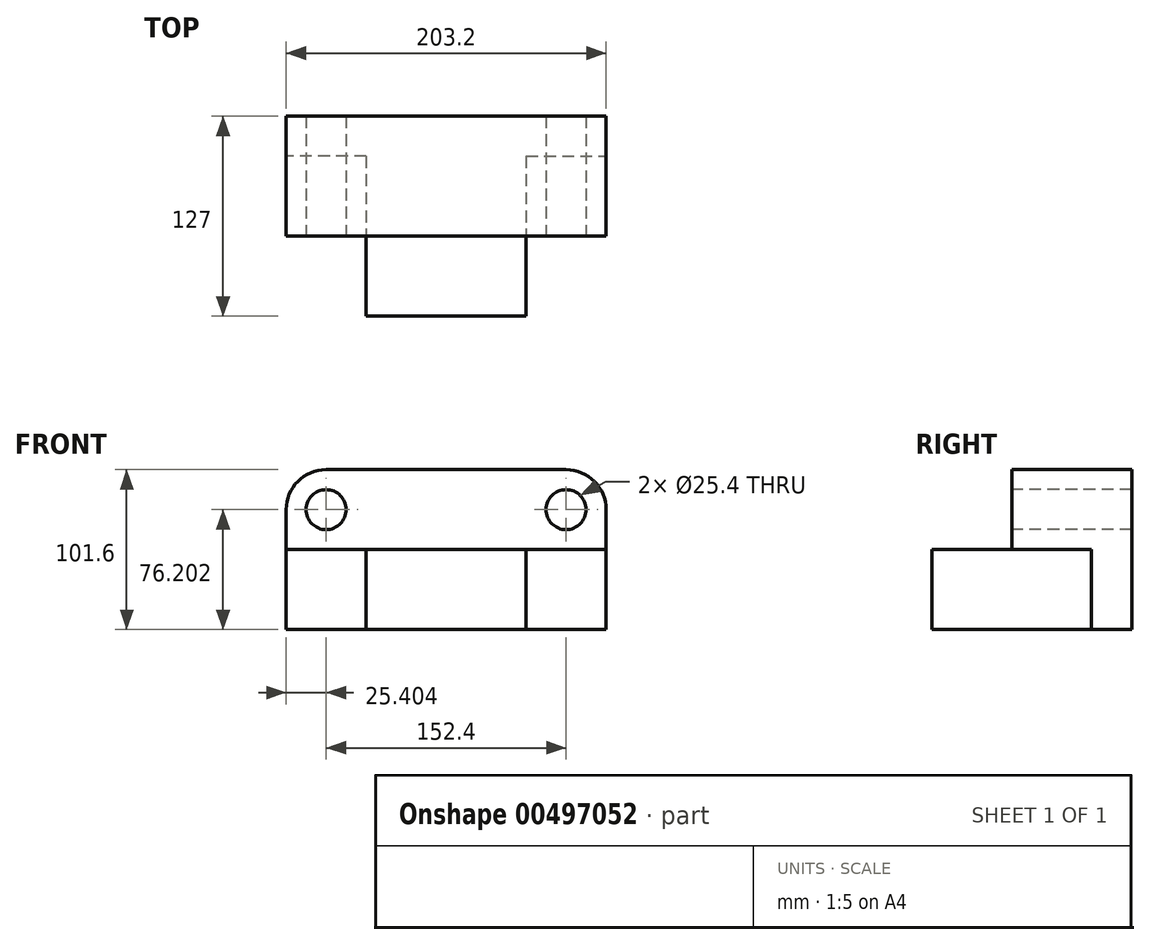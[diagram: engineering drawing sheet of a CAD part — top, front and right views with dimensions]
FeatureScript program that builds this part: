
annotation { "Feature Type Name" : "Feature", "Feature Type Description" : "" }
export const myFeature = defineFeature(function(context is Context, id is Id, definition is map)
    precondition{}
    {
        {
            var Q0;
            Q0=qCreatedBy(makeId("Front.planeOp"),FACE);
            var sketch = newSketch(context, id + "F0", { "sketchPlane" : qUnion([Q0])});
            skLineSegment(sketch, "E0", {"start": v(-74.58, -52.28) * mm, "end": v(128.62, -52.28) * mm});
            skLineSegment(sketch, "E1", {"start": v(128.62, -52.28) * mm, "end": v(128.62, 49.32) * mm});
            skLineSegment(sketch, "E2", {"start": v(128.62, 49.32) * mm, "end": v(-74.58, 49.32) * mm});
            skLineSegment(sketch, "E3", {"start": v(-74.58, 49.32) * mm, "end": v(-74.58, -52.28) * mm});
            skSolve(sketch);
        }
        {
            var Q0;
            Q0=makeQuery(id+"F0.imprint","IMPRINT",FACE,{"disambiguationData":[TD([[makeQuery(id+"F0.imprint","IMPRINT",EDGE,{"derivedFrom":sQuery(id+"F0.wireOp",EDGE,"E0")}),1.0]])]});
            extrude(context, id + "F1", {"entities" : qUnion([Q0]), "depth" : 76.2 * mm});
        }
        {
            var Q0;
            Q0=makeQuery(id+"F1.opExtrude","CAP_FACE",FACE,{"disambiguationData":[OSD([sQuery(id+"F0.wireOp",EDGE,"E0"),sQuery(id+"F0.wireOp",EDGE,"E1"),sQuery(id+"F0.wireOp",EDGE,"E2"),sQuery(id+"F0.wireOp",EDGE,"E3")])],"isStart":false});
            var sketch = newSketch(context, id + "F2", { "sketchPlane" : qUnion([Q0])});
            skLineSegment(sketch, "E4", {"start": v(128.62, -52.28) * mm, "end": v(77.82, -52.28) * mm});
            skLineSegment(sketch, "E5", {"start": v(77.82, -52.28) * mm, "end": v(77.82, -1.48) * mm});
            skLineSegment(sketch, "E6", {"start": v(77.82, -1.48) * mm, "end": v(128.62, -1.48) * mm});
            skLineSegment(sketch, "E7", {"start": v(128.62, -1.48) * mm, "end": v(128.62, -52.28) * mm});
            skLineSegment(sketch, "E8", {"start": v(-74.58, -52.28) * mm, "end": v(-23.78, -52.28) * mm});
            skLineSegment(sketch, "E9", {"start": v(-23.78, -52.28) * mm, "end": v(-23.78, -1.48) * mm});
            skLineSegment(sketch, "E10", {"start": v(-23.78, -1.48) * mm, "end": v(-74.58, -1.48) * mm});
            skLineSegment(sketch, "E11", {"start": v(-74.58, -1.48) * mm, "end": v(-74.58, -52.28) * mm});
            skSolve(sketch);
        }
        {
            var Q0;
            Q0=makeQuery(id+"F1.opExtrude","CAP_FACE",FACE,{"disambiguationData":[OSD([sQuery(id+"F0.wireOp",EDGE,"E0"),sQuery(id+"F0.wireOp",EDGE,"E1"),sQuery(id+"F0.wireOp",EDGE,"E2"),sQuery(id+"F0.wireOp",EDGE,"E3")])],"isStart":true});
            extrude(context, id + "F3", {"entities" : qUnion([Q0]), "operationType" : NewBodyOperationType.ADD, "depth" : 25.4 * mm});
        }
        {
            var Q0;
            Q0=makeQuery(id+"F2.imprint","IMPRINT",FACE,{"disambiguationData":[TD([[makeQuery(id+"F2.imprint","IMPRINT",EDGE,{"derivedFrom":sQuery(id+"F2.wireOp",EDGE,"E4")}),1.0]])]});
            var Q1;
            Q1=makeQuery(id+"F2.imprint","IMPRINT",FACE,{"disambiguationData":[TD([[makeQuery(id+"F2.imprint","IMPRINT",EDGE,{"derivedFrom":sQuery(id+"F2.wireOp",EDGE,"E8")}),1.0]])]});
            extrude(context, id + "F4", {"entities" : qUnion([Q0, Q1]), "operationType" : NewBodyOperationType.REMOVE, "oppositeDirection" : true, "depth" : 76.2 * mm});
        }
        {
            var Q0;
            {var subQ0=sQuery(id+"F0.wireOp",EDGE,"E1");Q0=makeQuery(id+"F3.boolean.opBoolean","MERGE",FACE,{"derivedFrom":[makeQuery(id+"F1.opExtrude","SWEPT_FACE",FACE,{"disambiguationData":[OSD([subQ0])]}),makeQuery(id+"F3.opExtrude","SWEPT_FACE",FACE,{"disambiguationData":[OSD([subQ0])]})]});}
            var sketch = newSketch(context, id + "F5", { "sketchPlane" : qUnion([Q0])});
            skLineSegment(sketch, "E12", {"start": v(-76.2, -1.48) * mm, "end": v(-50.8, -1.48) * mm});
            skLineSegment(sketch, "E13", {"start": v(-50.8, -1.48) * mm, "end": v(-50.8, 49.32) * mm});
            skLineSegment(sketch, "E14", {"start": v(-50.8, 49.32) * mm, "end": v(-76.2, 49.32) * mm});
            skLineSegment(sketch, "E15", {"start": v(-76.2, 49.32) * mm, "end": v(-76.2, -1.48) * mm});
            skSolve(sketch);
        }
        {
            var Q0;
            Q0=makeQuery(id+"F5.imprint","IMPRINT",FACE,{"disambiguationData":[TD([[makeQuery(id+"F5.imprint","IMPRINT",EDGE,{"derivedFrom":sQuery(id+"F5.wireOp",EDGE,"E12")}),-1.0]])]});
            extrude(context, id + "F6", {"entities" : qUnion([Q0]), "operationType" : NewBodyOperationType.REMOVE, "oppositeDirection" : true, "depth" : 203.2 * mm});
        }
        {
            var Q0;
            Q0=makeQuery(id+"F1.opExtrude","CAP_FACE",FACE,{"disambiguationData":[OSD([sQuery(id+"F0.wireOp",EDGE,"E0"),sQuery(id+"F0.wireOp",EDGE,"E1"),sQuery(id+"F0.wireOp",EDGE,"E2"),sQuery(id+"F0.wireOp",EDGE,"E3")])],"isStart":false});
            extrude(context, id + "F7", {"entities" : qUnion([Q0]), "operationType" : NewBodyOperationType.ADD, "depth" : 25.4 * mm});
        }
        {
            var Q0;
            Q0=makeQuery(id+"F6.boolean.opBoolean","COPY",FACE,{"derivedFrom":makeQuery(id+"F6.opExtrude","SWEPT_FACE",FACE,{"disambiguationData":[OSD([sQuery(id+"F5.wireOp",EDGE,"E13")])]})});
            var sketch = newSketch(context, id + "F8", { "sketchPlane" : qUnion([Q0])});
            skLineSegment(sketch, "E16", {"start": v(-74.58, 49.32) * mm, "end": v(-74.58, 23.92) * mm});
            skLineSegment(sketch, "E17", {"start": v(128.62, 49.32) * mm, "end": v(128.62, 23.92) * mm});
            skLineSegment(sketch, "E18", {"start": v(-74.58, 49.32) * mm, "end": v(-49.18, 49.32) * mm});
            skLineSegment(sketch, "E19", {"start": v(128.62, 49.32) * mm, "end": v(103.22, 49.32) * mm});
            skArc(sketch, "E20", {"start": v(-49.18, 49.32) * mm, "mid": v(-67.14, 41.88) * mm, "end": v(-74.58, 23.92) * mm});
            skArc(sketch, "E21", {"start": v(128.62, 23.92) * mm, "mid": v(121.18, 41.88) * mm, "end": v(103.22, 49.32) * mm});
            skSolve(sketch);
        }
        {
            var Q0;
            Q0=makeQuery(id+"F8.imprint","IMPRINT",FACE,{"disambiguationData":[TD([[makeQuery(id+"F8.imprint","IMPRINT",EDGE,{"derivedFrom":sQuery(id+"F8.wireOp",EDGE,"E17")}),1.0]])]});
            var Q1;
            Q1=makeQuery(id+"F8.imprint","IMPRINT",FACE,{"disambiguationData":[TD([[makeQuery(id+"F8.imprint","IMPRINT",EDGE,{"derivedFrom":sQuery(id+"F8.wireOp",EDGE,"E16")}),-1.0]])]});
            extrude(context, id + "F9", {"entities" : qUnion([Q0, Q1]), "operationType" : NewBodyOperationType.REMOVE, "oppositeDirection" : true, "depth" : 76.2 * mm});
        }
        {
            var Q0;
            Q0=makeQuery(id+"F6.boolean.opBoolean","COPY",FACE,{"derivedFrom":makeQuery(id+"F6.opExtrude","SWEPT_FACE",FACE,{"disambiguationData":[OSD([sQuery(id+"F5.wireOp",EDGE,"E13")])]})});
            var sketch = newSketch(context, id + "F10", { "sketchPlane" : qUnion([Q0])});
            skLineSegment(sketch, "E22", {"start": v(-49.18, 49.32) * mm, "end": v(-49.18, 23.92) * mm});
            skLineSegment(sketch, "E23", {"start": v(103.22, 49.32) * mm, "end": v(103.22, 23.92) * mm});
            skCircle(sketch, "E24", {"center": v(-49.18, 23.92) * mm, "radius": 12.7 * mm});
            skCircle(sketch, "E25", {"center": v(103.22, 23.92) * mm, "radius": 12.7 * mm});
            skSolve(sketch);
        }
        {
            var Q0;
            Q0=makeQuery(id+"F10.imprint","IMPRINT",FACE,{"disambiguationData":[TD([[makeQuery(id+"F10.imprint","IMPRINT",EDGE,{"derivedFrom":sQuery(id+"F10.wireOp",EDGE,"E24")}),1.0]])]});
            var Q1;
            Q1=makeQuery(id+"F10.imprint","IMPRINT",FACE,{"disambiguationData":[TD([[makeQuery(id+"F10.imprint","IMPRINT",EDGE,{"derivedFrom":sQuery(id+"F10.wireOp",EDGE,"E25")}),1.0]])]});
            extrude(context, id + "F11", {"entities" : qUnion([Q0, Q1]), "operationType" : NewBodyOperationType.REMOVE, "oppositeDirection" : true, "depth" : 76.2 * mm});
        }
    });
